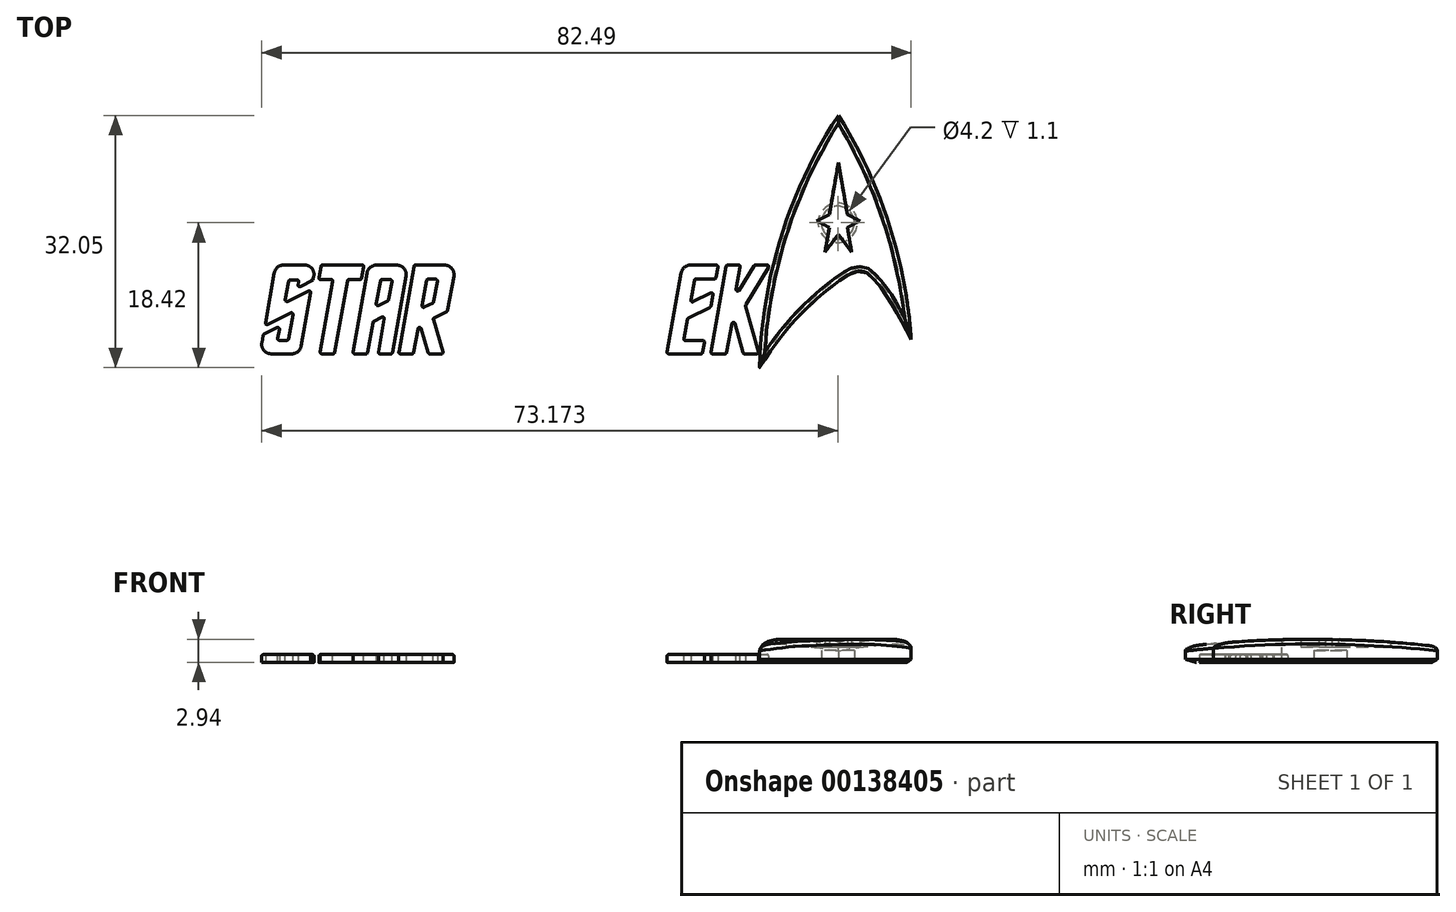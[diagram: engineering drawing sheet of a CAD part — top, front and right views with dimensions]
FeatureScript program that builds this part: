
annotation { "Feature Type Name" : "Feature", "Feature Type Description" : "" }
export const myFeature = defineFeature(function(context is Context, id is Id, definition is map)
    precondition{}
    {
        {
            var Q0;
            Q0=qCreatedBy(makeId("Top.planeOp"),FACE);
            var sketch = newSketch(context, id + "F0", { "sketchPlane" : qUnion([Q0])});
            skLineSegment(sketch, "E0", {"start": v(-63.47, 1.77) * mm, "end": v(-63.04, 4.22) * mm});
            skLineSegment(sketch, "E1", {"start": v(-61.48, 13.05) * mm, "end": v(-56.38, 13.05) * mm});
            skLineSegment(sketch, "E2", {"start": v(-56.38, 13.05) * mm, "end": v(-56.71, 11.14) * mm});
            skLineSegment(sketch, "E3", {"start": v(-56.71, 11.14) * mm, "end": v(-58.7, 10.14) * mm});
            skLineSegment(sketch, "E4", {"start": v(-58.7, 10.14) * mm, "end": v(-58.52, 11.14) * mm});
            skLineSegment(sketch, "E5", {"start": v(-58.52, 11.14) * mm, "end": v(-59.8, 11.14) * mm});
            skLineSegment(sketch, "E6", {"start": v(-59.8, 11.14) * mm, "end": v(-60.32, 8.24) * mm});
            skLineSegment(sketch, "E7", {"start": v(-60.32, 8.24) * mm, "end": v(-56.96, 9.93) * mm});
            skLineSegment(sketch, "E8", {"start": v(-56.96, 9.93) * mm, "end": v(-58.4, 1.77) * mm});
            skLineSegment(sketch, "E9", {"start": v(-58.4, 1.77) * mm, "end": v(-63.47, 1.77) * mm});
            skLineSegment(sketch, "E10", {"start": v(-59.86, 3.49) * mm, "end": v(-59.21, 7.15) * mm});
            skLineSegment(sketch, "E11", {"start": v(-59.21, 7.15) * mm, "end": v(-62.85, 5.31) * mm});
            skLineSegment(sketch, "E12", {"start": v(-63.04, 4.22) * mm, "end": v(-60.94, 5.28) * mm});
            skLineSegment(sketch, "E13", {"start": v(-60.94, 5.28) * mm, "end": v(-61.25, 3.49) * mm});
            skLineSegment(sketch, "E14", {"start": v(-61.25, 3.49) * mm, "end": v(-59.86, 3.49) * mm});
            skLineSegment(sketch, "E15", {"start": v(-55.7, 13.04) * mm, "end": v(-57.69, 1.77) * mm});
            skLineSegment(sketch, "E16", {"start": v(-55.85, 1.77) * mm, "end": v(-54, 1.77) * mm});
            skLineSegment(sketch, "E17", {"start": v(-52.25, 1.77) * mm, "end": v(-50.25, 13.04) * mm});
            skLineSegment(sketch, "E18", {"start": v(-55.7, 13.04) * mm, "end": v(-50.25, 13.04) * mm});
            skLineSegment(sketch, "E19", {"start": v(-55.85, 1.77) * mm, "end": v(-54.18, 11.21) * mm});
            skLineSegment(sketch, "E20", {"start": v(-54.18, 11.21) * mm, "end": v(-56.02, 11.21) * mm});
            skLineSegment(sketch, "E21", {"start": v(-54, 1.77) * mm, "end": v(-52.32, 11.21) * mm});
            skLineSegment(sketch, "E22", {"start": v(-52.32, 11.21) * mm, "end": v(-50.57, 11.21) * mm});
            skLineSegment(sketch, "E23", {"start": v(-51.68, 1.77) * mm, "end": v(-49.68, 13.04) * mm});
            skLineSegment(sketch, "E24", {"start": v(-49.68, 13.04) * mm, "end": v(-44.67, 13.04) * mm});
            skLineSegment(sketch, "E25", {"start": v(-44.67, 13.04) * mm, "end": v(-46.66, 1.77) * mm});
            skLineSegment(sketch, "E26", {"start": v(-46.66, 1.77) * mm, "end": v(-48.47, 1.77) * mm});
            skLineSegment(sketch, "E27", {"start": v(-45.87, 1.77) * mm, "end": v(-43.87, 13.04) * mm});
            skLineSegment(sketch, "E28", {"start": v(-43.87, 13.04) * mm, "end": v(-38.6, 13.04) * mm});
            skLineSegment(sketch, "E29", {"start": v(-38.6, 13.04) * mm, "end": v(-39.63, 7.21) * mm});
            skLineSegment(sketch, "E30", {"start": v(-40.42, 2.74) * mm, "end": v(-40.12, 1.77) * mm});
            skLineSegment(sketch, "E31", {"start": v(-40.12, 1.77) * mm, "end": v(-42.07, 1.77) * mm});
            skLineSegment(sketch, "E32", {"start": v(-40.42, 2.74) * mm, "end": v(-41.5, 6.27) * mm});
            skLineSegment(sketch, "E33", {"start": v(-49.82, 1.77) * mm, "end": v(-49.1, 5.85) * mm});
            skLineSegment(sketch, "E34", {"start": v(-49.1, 5.85) * mm, "end": v(-47.61, 6.6) * mm});
            skLineSegment(sketch, "E35", {"start": v(-47.61, 6.6) * mm, "end": v(-48.47, 1.77) * mm});
            skLineSegment(sketch, "E36", {"start": v(-41.5, 6.27) * mm, "end": v(-39.63, 7.21) * mm});
            skLineSegment(sketch, "E37", {"start": v(-43.26, 5.78) * mm, "end": v(-43.97, 1.77) * mm});
            skLineSegment(sketch, "E38", {"start": v(-42.07, 1.77) * mm, "end": v(-43.26, 5.78) * mm});
            skLineSegment(sketch, "E39", {"start": v(-42.95, 7.51) * mm, "end": v(-41.41, 8.3) * mm});
            skLineSegment(sketch, "E40", {"start": v(-41.41, 8.3) * mm, "end": v(-40.9, 11.24) * mm});
            skLineSegment(sketch, "E41", {"start": v(-42.95, 7.51) * mm, "end": v(-42.3, 11.24) * mm});
            skLineSegment(sketch, "E42", {"start": v(-42.3, 11.24) * mm, "end": v(-40.9, 11.24) * mm});
            skLineSegment(sketch, "E43.trimOffspring", {"start": v(-43.97, 1.77) * mm, "end": v(-45.87, 1.77) * mm});
            skLineSegment(sketch, "E44", {"start": v(-48.76, 7.72) * mm, "end": v(-48.15, 11.21) * mm});
            skLineSegment(sketch, "E45", {"start": v(-48.15, 11.21) * mm, "end": v(-46.67, 11.21) * mm});
            skLineSegment(sketch, "E46", {"start": v(-46.67, 11.21) * mm, "end": v(-47.15, 8.54) * mm});
            skLineSegment(sketch, "E47", {"start": v(-48.76, 7.72) * mm, "end": v(-47.15, 8.54) * mm});
            skLineSegment(sketch, "E48.trimOffspring", {"start": v(-62.85, 5.31) * mm, "end": v(-61.48, 13.05) * mm});
            skLineSegment(sketch, "E49.trimOffspring", {"start": v(-49.82, 1.77) * mm, "end": v(-51.68, 1.77) * mm});
            skLineSegment(sketch, "E50", {"start": v(-9.8, 13.04) * mm, "end": v(-11.8, 1.77) * mm});
            skLineSegment(sketch, "E51", {"start": v(-11.8, 1.77) * mm, "end": v(-7.25, 1.77) * mm});
            skLineSegment(sketch, "E52", {"start": v(-7.25, 1.77) * mm, "end": v(-6.95, 3.45) * mm});
            skLineSegment(sketch, "E53", {"start": v(-5.26, 13.04) * mm, "end": v(-9.8, 13.04) * mm});
            skLineSegment(sketch, "E54", {"start": v(-6.23, 1.77) * mm, "end": v(-4.23, 13.04) * mm});
            skLineSegment(sketch, "E55", {"start": v(-4.23, 13.04) * mm, "end": v(-2.43, 13.04) * mm});
            skLineSegment(sketch, "E56", {"start": v(-0.45, 3.06) * mm, "end": v(-0.1, 1.77) * mm});
            skLineSegment(sketch, "E57", {"start": v(-0.1, 1.77) * mm, "end": v(-2.08, 1.77) * mm});
            skLineSegment(sketch, "E58", {"start": v(-0.45, 3.06) * mm, "end": v(-1.79, 7.94) * mm});
            skLineSegment(sketch, "E59", {"start": v(-1.79, 7.94) * mm, "end": v(1.32, 13.04) * mm});
            skLineSegment(sketch, "E60", {"start": v(-0.64, 13.04) * mm, "end": v(-3.16, 8.91) * mm});
            skLineSegment(sketch, "E61", {"start": v(-3.16, 8.91) * mm, "end": v(-2.43, 13.04) * mm});
            skLineSegment(sketch, "E62", {"start": v(-4.2, 1.77) * mm, "end": v(-3.37, 6.47) * mm});
            skLineSegment(sketch, "E63", {"start": v(-3.37, 6.47) * mm, "end": v(-2.08, 1.77) * mm});
            skLineSegment(sketch, "E64", {"start": v(-6.95, 3.45) * mm, "end": v(-9.64, 3.45) * mm});
            skLineSegment(sketch, "E65", {"start": v(-9.64, 3.45) * mm, "end": v(-9.14, 6.27) * mm});
            skLineSegment(sketch, "E66", {"start": v(-9.14, 6.27) * mm, "end": v(-6.2, 7.72) * mm});
            skLineSegment(sketch, "E67", {"start": v(-9.14, 6.27) * mm, "end": v(-8.26, 11.26) * mm});
            skLineSegment(sketch, "E68", {"start": v(-8.26, 11.26) * mm, "end": v(-5.57, 11.26) * mm});
            skLineSegment(sketch, "E69", {"start": v(-8.8, 8.2) * mm, "end": v(-5.85, 9.67) * mm});
            skLineSegment(sketch, "E70.trimOffspring", {"start": v(-5.57, 11.26) * mm, "end": v(-5.26, 13.04) * mm});
            skLineSegment(sketch, "E71.trimOffspring", {"start": v(-6.2, 7.72) * mm, "end": v(-5.85, 9.67) * mm});
            skLineSegment(sketch, "E72.trimOffspring", {"start": v(-4.2, 1.77) * mm, "end": v(-6.23, 1.77) * mm});
            skLineSegment(sketch, "E73.trimOffspring", {"start": v(-0.64, 13.04) * mm, "end": v(1.32, 13.04) * mm});
            skSolve(sketch);
        }
        {
            var Q0;
            Q0 = qSketchRegion(id + "F0", true);
            extrude(context, id + "F1", {"entities" : qUnion([Q0]), "depth" : 1 * mm, "offsetDistance" : 25 * mm});
        }
        {
            var Q0;
            Q0=makeQuery(id+"F1.opExtrude","SWEPT_EDGE",EDGE,{"disambiguationData":[OSD([sQuery(id+"F0.wireOp",EDGE,"E8"),sQuery(id+"F0.wireOp",EDGE,"E9")])]});
            var Q1;
            Q1=makeQuery(id+"F1.opExtrude","SWEPT_EDGE",EDGE,{"disambiguationData":[OSD([sQuery(id+"F0.wireOp",EDGE,"E0"),sQuery(id+"F0.wireOp",EDGE,"E9")])]});
            var Q2;
            Q2=makeQuery(id+"F1.opExtrude","SWEPT_EDGE",EDGE,{"disambiguationData":[OSD([sQuery(id+"F0.wireOp",EDGE,"E1"),sQuery(id+"F0.wireOp",EDGE,"E48.trimOffspring")])]});
            var Q3;
            Q3=makeQuery(id+"F1.opExtrude","SWEPT_EDGE",EDGE,{"disambiguationData":[OSD([sQuery(id+"F0.wireOp",EDGE,"E1"),sQuery(id+"F0.wireOp",EDGE,"E2")])]});
            var Q4;
            Q4=makeQuery(id+"F1.opExtrude","SWEPT_EDGE",EDGE,{"disambiguationData":[OSD([sQuery(id+"F0.wireOp",EDGE,"E23"),sQuery(id+"F0.wireOp",EDGE,"E24")])]});
            var Q5;
            Q5=makeQuery(id+"F1.opExtrude","SWEPT_EDGE",EDGE,{"disambiguationData":[OSD([sQuery(id+"F0.wireOp",EDGE,"E24"),sQuery(id+"F0.wireOp",EDGE,"E25")])]});
            var Q6;
            Q6=makeQuery(id+"F1.opExtrude","SWEPT_EDGE",EDGE,{"disambiguationData":[OSD([sQuery(id+"F0.wireOp",EDGE,"E28"),sQuery(id+"F0.wireOp",EDGE,"E29")])]});
            var Q7;
            Q7=makeQuery(id+"F1.opExtrude","SWEPT_EDGE",EDGE,{"disambiguationData":[OSD([sQuery(id+"F0.wireOp",EDGE,"E50"),sQuery(id+"F0.wireOp",EDGE,"E53")])]});
            fillet(context, id + "F2", {"entities" : qUnion([Q0, Q1, Q2, Q3, Q4, Q5, Q6, Q7]), "tangentPropagation" : true, "radius" : 1.2 * mm, "defaultsChanged" : false, "vertexSettings" : [], "allowEdgeOverflow" : false});
        }
        {
            var Q0;
            Q0=makeQuery(id+"F1.opExtrude","SWEPT_EDGE",EDGE,{"disambiguationData":[OSD([sQuery(id+"F0.wireOp",EDGE,"E7"),sQuery(id+"F0.wireOp",EDGE,"E8")])]});
            var Q1;
            Q1=makeQuery(id+"F1.opExtrude","SWEPT_EDGE",EDGE,{"disambiguationData":[OSD([sQuery(id+"F0.wireOp",EDGE,"E3"),sQuery(id+"F0.wireOp",EDGE,"E4")])]});
            var Q2;
            Q2=makeQuery(id+"F1.opExtrude","SWEPT_EDGE",EDGE,{"disambiguationData":[OSD([sQuery(id+"F0.wireOp",EDGE,"E5"),sQuery(id+"F0.wireOp",EDGE,"E6")])]});
            var Q3;
            Q3=makeQuery(id+"F1.opExtrude","SWEPT_EDGE",EDGE,{"disambiguationData":[OSD([sQuery(id+"F0.wireOp",EDGE,"E6"),sQuery(id+"F0.wireOp",EDGE,"E7")])]});
            var Q4;
            Q4=makeQuery(id+"F1.opExtrude","SWEPT_EDGE",EDGE,{"disambiguationData":[OSD([sQuery(id+"F0.wireOp",EDGE,"E13"),sQuery(id+"F0.wireOp",EDGE,"E14")])]});
            var Q5;
            Q5=makeQuery(id+"F1.opExtrude","SWEPT_EDGE",EDGE,{"disambiguationData":[OSD([sQuery(id+"F0.wireOp",EDGE,"E12"),sQuery(id+"F0.wireOp",EDGE,"E13")])]});
            var Q6;
            Q6=makeQuery(id+"F1.opExtrude","SWEPT_EDGE",EDGE,{"disambiguationData":[OSD([sQuery(id+"F0.wireOp",EDGE,"E0"),sQuery(id+"F0.wireOp",EDGE,"E12")])]});
            var Q7;
            Q7=makeQuery(id+"F1.opExtrude","SWEPT_EDGE",EDGE,{"disambiguationData":[OSD([sQuery(id+"F0.wireOp",EDGE,"E10"),sQuery(id+"F0.wireOp",EDGE,"E14")])]});
            var Q8;
            Q8=makeQuery(id+"F1.opExtrude","SWEPT_EDGE",EDGE,{"disambiguationData":[OSD([sQuery(id+"F0.wireOp",EDGE,"E10"),sQuery(id+"F0.wireOp",EDGE,"E11")])]});
            var Q9;
            Q9=makeQuery(id+"F1.opExtrude","SWEPT_EDGE",EDGE,{"disambiguationData":[OSD([sQuery(id+"F0.wireOp",EDGE,"E11"),sQuery(id+"F0.wireOp",EDGE,"E48.trimOffspring")])]});
            var Q10;
            Q10=makeQuery(id+"F1.opExtrude","SWEPT_EDGE",EDGE,{"disambiguationData":[OSD([sQuery(id+"F0.wireOp",EDGE,"E4"),sQuery(id+"F0.wireOp",EDGE,"E5")])]});
            var Q11;
            Q11=makeQuery(id+"F1.opExtrude","SWEPT_EDGE",EDGE,{"disambiguationData":[OSD([sQuery(id+"F0.wireOp",EDGE,"E15"),sQuery(id+"F0.wireOp",EDGE,"E18")])]});
            var Q12;
            Q12=makeQuery(id+"F1.opExtrude","SWEPT_EDGE",EDGE,{"disambiguationData":[OSD([sQuery(id+"F0.wireOp",EDGE,"E15"),sQuery(id+"F0.wireOp",EDGE,"E20")])]});
            var Q13;
            Q13=makeQuery(id+"F1.opExtrude","SWEPT_EDGE",EDGE,{"disambiguationData":[OSD([sQuery(id+"F0.wireOp",EDGE,"E19"),sQuery(id+"F0.wireOp",EDGE,"E20")])]});
            var Q14;
            Q14=makeQuery(id+"F1.opExtrude","SWEPT_EDGE",EDGE,{"disambiguationData":[OSD([sQuery(id+"F0.wireOp",EDGE,"E16"),sQuery(id+"F0.wireOp",EDGE,"E19")])]});
            var Q15;
            Q15=makeQuery(id+"F1.opExtrude","SWEPT_EDGE",EDGE,{"disambiguationData":[OSD([sQuery(id+"F0.wireOp",EDGE,"E16"),sQuery(id+"F0.wireOp",EDGE,"E21")])]});
            var Q16;
            Q16=makeQuery(id+"F1.opExtrude","SWEPT_EDGE",EDGE,{"disambiguationData":[OSD([sQuery(id+"F0.wireOp",EDGE,"E21"),sQuery(id+"F0.wireOp",EDGE,"E22")])]});
            var Q17;
            Q17=makeQuery(id+"F1.opExtrude","SWEPT_EDGE",EDGE,{"disambiguationData":[OSD([sQuery(id+"F0.wireOp",EDGE,"E17"),sQuery(id+"F0.wireOp",EDGE,"E22")])]});
            var Q18;
            Q18=makeQuery(id+"F1.opExtrude","SWEPT_EDGE",EDGE,{"disambiguationData":[OSD([sQuery(id+"F0.wireOp",EDGE,"E17"),sQuery(id+"F0.wireOp",EDGE,"E18")])]});
            var Q19;
            Q19=makeQuery(id+"F1.opExtrude","SWEPT_EDGE",EDGE,{"disambiguationData":[OSD([sQuery(id+"F0.wireOp",EDGE,"E44"),sQuery(id+"F0.wireOp",EDGE,"E45")])]});
            var Q20;
            Q20=makeQuery(id+"F1.opExtrude","SWEPT_EDGE",EDGE,{"disambiguationData":[OSD([sQuery(id+"F0.wireOp",EDGE,"E23"),sQuery(id+"F0.wireOp",EDGE,"E49.trimOffspring")])]});
            var Q21;
            Q21=makeQuery(id+"F1.opExtrude","SWEPT_EDGE",EDGE,{"disambiguationData":[OSD([sQuery(id+"F0.wireOp",EDGE,"E26"),sQuery(id+"F0.wireOp",EDGE,"E35")])]});
            var Q22;
            Q22=makeQuery(id+"F1.opExtrude","SWEPT_EDGE",EDGE,{"disambiguationData":[OSD([sQuery(id+"F0.wireOp",EDGE,"E33"),sQuery(id+"F0.wireOp",EDGE,"E49.trimOffspring")])]});
            var Q23;
            Q23=makeQuery(id+"F1.opExtrude","SWEPT_EDGE",EDGE,{"disambiguationData":[OSD([sQuery(id+"F0.wireOp",EDGE,"E33"),sQuery(id+"F0.wireOp",EDGE,"E34")])]});
            var Q24;
            Q24=makeQuery(id+"F1.opExtrude","SWEPT_EDGE",EDGE,{"disambiguationData":[OSD([sQuery(id+"F0.wireOp",EDGE,"E34"),sQuery(id+"F0.wireOp",EDGE,"E35")])]});
            var Q25;
            Q25=makeQuery(id+"F1.opExtrude","SWEPT_EDGE",EDGE,{"disambiguationData":[OSD([sQuery(id+"F0.wireOp",EDGE,"E25"),sQuery(id+"F0.wireOp",EDGE,"E26")])]});
            var Q26;
            Q26=makeQuery(id+"F1.opExtrude","SWEPT_EDGE",EDGE,{"disambiguationData":[OSD([sQuery(id+"F0.wireOp",EDGE,"E46"),sQuery(id+"F0.wireOp",EDGE,"E47")])]});
            var Q27;
            Q27=makeQuery(id+"F1.opExtrude","SWEPT_EDGE",EDGE,{"disambiguationData":[OSD([sQuery(id+"F0.wireOp",EDGE,"E45"),sQuery(id+"F0.wireOp",EDGE,"E46")])]});
            var Q28;
            Q28=makeQuery(id+"F1.opExtrude","SWEPT_EDGE",EDGE,{"disambiguationData":[OSD([sQuery(id+"F0.wireOp",EDGE,"E44"),sQuery(id+"F0.wireOp",EDGE,"E47")])]});
            var Q29;
            Q29=makeQuery(id+"F1.opExtrude","SWEPT_EDGE",EDGE,{"disambiguationData":[OSD([sQuery(id+"F0.wireOp",EDGE,"E27"),sQuery(id+"F0.wireOp",EDGE,"E43.trimOffspring")])]});
            var Q30;
            Q30=makeQuery(id+"F1.opExtrude","SWEPT_EDGE",EDGE,{"disambiguationData":[OSD([sQuery(id+"F0.wireOp",EDGE,"E37"),sQuery(id+"F0.wireOp",EDGE,"E43.trimOffspring")])]});
            var Q31;
            Q31=makeQuery(id+"F1.opExtrude","SWEPT_EDGE",EDGE,{"disambiguationData":[OSD([sQuery(id+"F0.wireOp",EDGE,"E31"),sQuery(id+"F0.wireOp",EDGE,"E38")])]});
            var Q32;
            Q32=makeQuery(id+"F1.opExtrude","SWEPT_EDGE",EDGE,{"disambiguationData":[OSD([sQuery(id+"F0.wireOp",EDGE,"E30"),sQuery(id+"F0.wireOp",EDGE,"E31")])]});
            var Q33;
            Q33=makeQuery(id+"F1.opExtrude","SWEPT_EDGE",EDGE,{"disambiguationData":[OSD([sQuery(id+"F0.wireOp",EDGE,"E32"),sQuery(id+"F0.wireOp",EDGE,"E36")])]});
            var Q34;
            Q34=makeQuery(id+"F1.opExtrude","SWEPT_EDGE",EDGE,{"disambiguationData":[OSD([sQuery(id+"F0.wireOp",EDGE,"E29"),sQuery(id+"F0.wireOp",EDGE,"E36")])]});
            var Q35;
            Q35=makeQuery(id+"F1.opExtrude","SWEPT_EDGE",EDGE,{"disambiguationData":[OSD([sQuery(id+"F0.wireOp",EDGE,"E41"),sQuery(id+"F0.wireOp",EDGE,"E42")])]});
            var Q36;
            Q36=makeQuery(id+"F1.opExtrude","SWEPT_EDGE",EDGE,{"disambiguationData":[OSD([sQuery(id+"F0.wireOp",EDGE,"E37"),sQuery(id+"F0.wireOp",EDGE,"E38")])]});
            var Q37;
            Q37=makeQuery(id+"F1.opExtrude","SWEPT_EDGE",EDGE,{"disambiguationData":[OSD([sQuery(id+"F0.wireOp",EDGE,"E39"),sQuery(id+"F0.wireOp",EDGE,"E40")])]});
            var Q38;
            Q38=makeQuery(id+"F1.opExtrude","SWEPT_EDGE",EDGE,{"disambiguationData":[OSD([sQuery(id+"F0.wireOp",EDGE,"E39"),sQuery(id+"F0.wireOp",EDGE,"E41")])]});
            var Q39;
            Q39=makeQuery(id+"F1.opExtrude","SWEPT_EDGE",EDGE,{"disambiguationData":[OSD([sQuery(id+"F0.wireOp",EDGE,"E40"),sQuery(id+"F0.wireOp",EDGE,"E42")])]});
            var Q40;
            Q40=makeQuery(id+"F1.opExtrude","SWEPT_EDGE",EDGE,{"disambiguationData":[OSD([sQuery(id+"F0.wireOp",EDGE,"E27"),sQuery(id+"F0.wireOp",EDGE,"E28")])]});
            var Q41;
            Q41=makeQuery(id+"F1.opExtrude","SWEPT_EDGE",EDGE,{"disambiguationData":[OSD([sQuery(id+"F0.wireOp",EDGE,"E53"),sQuery(id+"F0.wireOp",EDGE,"E70.trimOffspring")])]});
            var Q42;
            Q42=makeQuery(id+"F1.opExtrude","SWEPT_EDGE",EDGE,{"disambiguationData":[OSD([sQuery(id+"F0.wireOp",EDGE,"E68"),sQuery(id+"F0.wireOp",EDGE,"E70.trimOffspring")])]});
            var Q43;
            Q43=makeQuery(id+"F1.opExtrude","SWEPT_EDGE",EDGE,{"disambiguationData":[OSD([sQuery(id+"F0.wireOp",EDGE,"E69"),sQuery(id+"F0.wireOp",EDGE,"E71.trimOffspring")])]});
            var Q44;
            Q44=makeQuery(id+"F1.opExtrude","SWEPT_EDGE",EDGE,{"disambiguationData":[OSD([sQuery(id+"F0.wireOp",EDGE,"E66"),sQuery(id+"F0.wireOp",EDGE,"E71.trimOffspring")])]});
            var Q45;
            Q45=makeQuery(id+"F1.opExtrude","SWEPT_EDGE",EDGE,{"disambiguationData":[OSD([sQuery(id+"F0.wireOp",EDGE,"E67"),sQuery(id+"F0.wireOp",EDGE,"E68")])]});
            var Q46;
            Q46=makeQuery(id+"F1.opExtrude","SWEPT_EDGE",EDGE,{"disambiguationData":[OSD([sQuery(id+"F0.wireOp",EDGE,"E67"),sQuery(id+"F0.wireOp",EDGE,"E69")])]});
            var Q47;
            Q47=makeQuery(id+"F1.opExtrude","SWEPT_EDGE",EDGE,{"disambiguationData":[OSD([sQuery(id+"F0.wireOp",EDGE,"E65"),sQuery(id+"F0.wireOp",EDGE,"E66"),sQuery(id+"F0.wireOp",EDGE,"E67")])]});
            var Q48;
            Q48=makeQuery(id+"F1.opExtrude","SWEPT_EDGE",EDGE,{"disambiguationData":[OSD([sQuery(id+"F0.wireOp",EDGE,"E52"),sQuery(id+"F0.wireOp",EDGE,"E64")])]});
            var Q49;
            Q49=makeQuery(id+"F1.opExtrude","SWEPT_EDGE",EDGE,{"disambiguationData":[OSD([sQuery(id+"F0.wireOp",EDGE,"E51"),sQuery(id+"F0.wireOp",EDGE,"E52")])]});
            var Q50;
            Q50=makeQuery(id+"F1.opExtrude","SWEPT_EDGE",EDGE,{"disambiguationData":[OSD([sQuery(id+"F0.wireOp",EDGE,"E50"),sQuery(id+"F0.wireOp",EDGE,"E51")])]});
            var Q51;
            Q51=makeQuery(id+"F1.opExtrude","SWEPT_EDGE",EDGE,{"disambiguationData":[OSD([sQuery(id+"F0.wireOp",EDGE,"E64"),sQuery(id+"F0.wireOp",EDGE,"E65")])]});
            var Q52;
            Q52=makeQuery(id+"F1.opExtrude","SWEPT_EDGE",EDGE,{"disambiguationData":[OSD([sQuery(id+"F0.wireOp",EDGE,"E62"),sQuery(id+"F0.wireOp",EDGE,"E63")])]});
            var Q53;
            Q53=makeQuery(id+"F1.opExtrude","SWEPT_EDGE",EDGE,{"disambiguationData":[OSD([sQuery(id+"F0.wireOp",EDGE,"E62"),sQuery(id+"F0.wireOp",EDGE,"E72.trimOffspring")])]});
            var Q54;
            Q54=makeQuery(id+"F1.opExtrude","SWEPT_EDGE",EDGE,{"disambiguationData":[OSD([sQuery(id+"F0.wireOp",EDGE,"E54"),sQuery(id+"F0.wireOp",EDGE,"E72.trimOffspring")])]});
            var Q55;
            Q55=makeQuery(id+"F1.opExtrude","SWEPT_EDGE",EDGE,{"disambiguationData":[OSD([sQuery(id+"F0.wireOp",EDGE,"E57"),sQuery(id+"F0.wireOp",EDGE,"E63")])]});
            var Q56;
            Q56=makeQuery(id+"F1.opExtrude","SWEPT_EDGE",EDGE,{"disambiguationData":[OSD([sQuery(id+"F0.wireOp",EDGE,"E56"),sQuery(id+"F0.wireOp",EDGE,"E57")])]});
            var Q57;
            Q57=makeQuery(id+"F1.opExtrude","SWEPT_EDGE",EDGE,{"disambiguationData":[OSD([sQuery(id+"F0.wireOp",EDGE,"E58"),sQuery(id+"F0.wireOp",EDGE,"E59")])]});
            var Q58;
            Q58=makeQuery(id+"F1.opExtrude","SWEPT_EDGE",EDGE,{"disambiguationData":[OSD([sQuery(id+"F0.wireOp",EDGE,"E59"),sQuery(id+"F0.wireOp",EDGE,"E73.trimOffspring")])]});
            var Q59;
            Q59=makeQuery(id+"F1.opExtrude","SWEPT_EDGE",EDGE,{"disambiguationData":[OSD([sQuery(id+"F0.wireOp",EDGE,"E60"),sQuery(id+"F0.wireOp",EDGE,"E73.trimOffspring")])]});
            var Q60;
            Q60=makeQuery(id+"F1.opExtrude","SWEPT_EDGE",EDGE,{"disambiguationData":[OSD([sQuery(id+"F0.wireOp",EDGE,"E60"),sQuery(id+"F0.wireOp",EDGE,"E61")])]});
            var Q61;
            Q61=makeQuery(id+"F1.opExtrude","SWEPT_EDGE",EDGE,{"disambiguationData":[OSD([sQuery(id+"F0.wireOp",EDGE,"E55"),sQuery(id+"F0.wireOp",EDGE,"E61")])]});
            var Q62;
            Q62=makeQuery(id+"F1.opExtrude","SWEPT_EDGE",EDGE,{"disambiguationData":[OSD([sQuery(id+"F0.wireOp",EDGE,"E54"),sQuery(id+"F0.wireOp",EDGE,"E55")])]});
            fillet(context, id + "F3", {"entities" : qUnion([Q0, Q1, Q2, Q3, Q4, Q5, Q6, Q7, Q8, Q9, Q10, Q11, Q12, Q13, Q14, Q15, Q16, Q17, Q18, Q19, Q20, Q21, Q22, Q23, Q24, Q25, Q26, Q27, Q28, Q29, Q30, Q31, Q32, Q33, Q34, Q35, Q36, Q37, Q38, Q39, Q40, Q41, Q42, Q43, Q44, Q45, Q46, Q47, Q48, Q49, Q50, Q51, Q52, Q53, Q54, Q55, Q56, Q57, Q58, Q59, Q60, Q61, Q62]), "tangentPropagation" : true, "radius" : 0.2 * mm, "defaultsChanged" : false, "vertexSettings" : [], "allowEdgeOverflow" : false});
        }
        {
            var Q0;
            Q0=makeQuery(id+"F1.opExtrude","CAP_FACE",FACE,{"disambiguationData":[OSD([sQuery(id+"F0.wireOp",EDGE,"E0"),sQuery(id+"F0.wireOp",EDGE,"E1"),sQuery(id+"F0.wireOp",EDGE,"E2"),sQuery(id+"F0.wireOp",EDGE,"E3"),sQuery(id+"F0.wireOp",EDGE,"E4"),sQuery(id+"F0.wireOp",EDGE,"E5"),sQuery(id+"F0.wireOp",EDGE,"E6"),sQuery(id+"F0.wireOp",EDGE,"E7"),sQuery(id+"F0.wireOp",EDGE,"E8"),sQuery(id+"F0.wireOp",EDGE,"E9"),sQuery(id+"F0.wireOp",EDGE,"E10"),sQuery(id+"F0.wireOp",EDGE,"E11"),sQuery(id+"F0.wireOp",EDGE,"E12"),sQuery(id+"F0.wireOp",EDGE,"E13"),sQuery(id+"F0.wireOp",EDGE,"E14"),sQuery(id+"F0.wireOp",EDGE,"E48.trimOffspring")])],"isStart":false});
            var Q1;
            Q1=makeQuery(id+"F1.opExtrude","CAP_FACE",FACE,{"disambiguationData":[OSD([sQuery(id+"F0.wireOp",EDGE,"E15"),sQuery(id+"F0.wireOp",EDGE,"E16"),sQuery(id+"F0.wireOp",EDGE,"E17"),sQuery(id+"F0.wireOp",EDGE,"E18"),sQuery(id+"F0.wireOp",EDGE,"E19"),sQuery(id+"F0.wireOp",EDGE,"E20"),sQuery(id+"F0.wireOp",EDGE,"E21"),sQuery(id+"F0.wireOp",EDGE,"E22")])],"isStart":false});
            var Q2;
            Q2=makeQuery(id+"F1.opExtrude","CAP_FACE",FACE,{"disambiguationData":[OSD([sQuery(id+"F0.wireOp",EDGE,"E23"),sQuery(id+"F0.wireOp",EDGE,"E24"),sQuery(id+"F0.wireOp",EDGE,"E25"),sQuery(id+"F0.wireOp",EDGE,"E26"),sQuery(id+"F0.wireOp",EDGE,"E33"),sQuery(id+"F0.wireOp",EDGE,"E34"),sQuery(id+"F0.wireOp",EDGE,"E35"),sQuery(id+"F0.wireOp",EDGE,"E44"),sQuery(id+"F0.wireOp",EDGE,"E45"),sQuery(id+"F0.wireOp",EDGE,"E46"),sQuery(id+"F0.wireOp",EDGE,"E47"),sQuery(id+"F0.wireOp",EDGE,"E49.trimOffspring")])],"isStart":false});
            var Q3;
            Q3=makeQuery(id+"F1.opExtrude","CAP_FACE",FACE,{"disambiguationData":[OSD([sQuery(id+"F0.wireOp",EDGE,"E27"),sQuery(id+"F0.wireOp",EDGE,"E28"),sQuery(id+"F0.wireOp",EDGE,"E29"),sQuery(id+"F0.wireOp",EDGE,"E30"),sQuery(id+"F0.wireOp",EDGE,"E31"),sQuery(id+"F0.wireOp",EDGE,"E32"),sQuery(id+"F0.wireOp",EDGE,"E36"),sQuery(id+"F0.wireOp",EDGE,"E37"),sQuery(id+"F0.wireOp",EDGE,"E38"),sQuery(id+"F0.wireOp",EDGE,"E39"),sQuery(id+"F0.wireOp",EDGE,"E40"),sQuery(id+"F0.wireOp",EDGE,"E41"),sQuery(id+"F0.wireOp",EDGE,"E42"),sQuery(id+"F0.wireOp",EDGE,"E43.trimOffspring")])],"isStart":false});
            var Q4;
            Q4=makeQuery(id+"F1.opExtrude","CAP_FACE",FACE,{"disambiguationData":[OSD([sQuery(id+"F0.wireOp",EDGE,"E50"),sQuery(id+"F0.wireOp",EDGE,"E51"),sQuery(id+"F0.wireOp",EDGE,"E52"),sQuery(id+"F0.wireOp",EDGE,"E53"),sQuery(id+"F0.wireOp",EDGE,"E64"),sQuery(id+"F0.wireOp",EDGE,"E65"),sQuery(id+"F0.wireOp",EDGE,"E66"),sQuery(id+"F0.wireOp",EDGE,"E67"),sQuery(id+"F0.wireOp",EDGE,"E68"),sQuery(id+"F0.wireOp",EDGE,"E69"),sQuery(id+"F0.wireOp",EDGE,"E70.trimOffspring"),sQuery(id+"F0.wireOp",EDGE,"E71.trimOffspring")])],"isStart":false});
            var Q5;
            Q5=makeQuery(id+"F1.opExtrude","CAP_FACE",FACE,{"disambiguationData":[OSD([sQuery(id+"F0.wireOp",EDGE,"E54"),sQuery(id+"F0.wireOp",EDGE,"E55"),sQuery(id+"F0.wireOp",EDGE,"E56"),sQuery(id+"F0.wireOp",EDGE,"E57"),sQuery(id+"F0.wireOp",EDGE,"E58"),sQuery(id+"F0.wireOp",EDGE,"E59"),sQuery(id+"F0.wireOp",EDGE,"E60"),sQuery(id+"F0.wireOp",EDGE,"E61"),sQuery(id+"F0.wireOp",EDGE,"E62"),sQuery(id+"F0.wireOp",EDGE,"E63"),sQuery(id+"F0.wireOp",EDGE,"E72.trimOffspring"),sQuery(id+"F0.wireOp",EDGE,"E73.trimOffspring")])],"isStart":false});
            fillet(context, id + "F4", {"entities" : qUnion([Q0, Q1, Q2, Q3, Q4, Q5]), "tangentPropagation" : true, "radius" : 0.2 * mm, "defaultsChanged" : false, "vertexSettings" : [], "allowEdgeOverflow" : false});
        }
        {
            var Q0;
            Q0=qCreatedBy(makeId("Top.planeOp"),FACE);
            var sketch = newSketch(context, id + "F5", { "sketchPlane" : qUnion([Q0])});
            skArc(sketch, "E74", {"start": v(10, 32.05) * mm, "mid": v(2.75, 16.73) * mm, "end": v(0, 0) * mm});
            skArc(sketch, "E75", {"start": v(19.25, 3.58) * mm, "mid": v(16.4, 18.4) * mm, "end": v(10, 32.05) * mm});
            skFitSpline(sketch, "E76", {"points": [v(19.25, 3.58) * mm, v(17.29, 7.18) * mm, v(15.43, 10.15) * mm, v(14.23, 11.51) * mm, v(13.29, 12.2) * mm, v(11.98, 12.12) * mm, v(10.29, 11.18) * mm, v(5.93, 7.51) * mm, v(2.46, 3.58) * mm, v(0, 0) * mm], "startDerivative": vector(-14.26, 27.94) * mm, "endDerivative": vector(-17.6, -27.28) * mm});
            skSolve(sketch);
        }
        {
            var Q0;
            Q0 = qSketchRegion(id + "F5", true);
            extrude(context, id + "F6", {"entities" : qUnion([Q0]), "depth" : 2 * mm, "offsetDistance" : 25 * mm});
        }
        {
            var Q0;
            Q0=qCreatedBy(makeId("Top.planeOp"),FACE);
            var sketch = newSketch(context, id + "F7", { "sketchPlane" : qUnion([Q0])});
            skArc(sketch, "E77", {"start": v(10, 32.05) * mm, "mid": v(2.75, 16.73) * mm, "end": v(0, 0) * mm});
            skArc(sketch, "E78", {"start": v(19.25, 3.58) * mm, "mid": v(16.4, 18.4) * mm, "end": v(10, 32.05) * mm});
            skFitSpline(sketch, "E79", {"points": [v(19.25, 3.58) * mm, v(17.29, 7.18) * mm, v(15.43, 10.15) * mm, v(14.23, 11.51) * mm, v(13.29, 12.2) * mm, v(11.98, 12.12) * mm, v(10.29, 11.18) * mm, v(5.93, 7.51) * mm, v(2.46, 3.58) * mm, v(0, 0) * mm], "startDerivative": vector(-14.26, 27.94) * mm, "endDerivative": vector(-17.6, -27.28) * mm});
            skLineSegment(sketch, "E80", {"start": v(10, 26.05) * mm, "end": v(11.15, 19.46) * mm});
            skLineSegment(sketch, "E81", {"start": v(11.15, 19.46) * mm, "end": v(12.75, 18.65) * mm});
            skLineSegment(sketch, "E82", {"start": v(12.75, 18.65) * mm, "end": v(11.15, 17.82) * mm});
            skLineSegment(sketch, "E83", {"start": v(11.15, 17.82) * mm, "end": v(11.7, 14.7) * mm});
            skLineSegment(sketch, "E84", {"start": v(11.7, 14.7) * mm, "end": v(10, 16.94) * mm});
            skLineSegment(sketch, "E85", {"start": v(10, 16.94) * mm, "end": v(10, 18.42) * mm});
            skLineSegment(sketch, "E86.MirrorCS", {"start": v(10, 26.05) * mm, "end": v(8.85, 19.46) * mm});
            skLineSegment(sketch, "E87.MirrorCS", {"start": v(8.85, 19.46) * mm, "end": v(7.25, 18.65) * mm});
            skLineSegment(sketch, "E88.MirrorCS", {"start": v(7.25, 18.65) * mm, "end": v(8.85, 17.82) * mm});
            skLineSegment(sketch, "E89.MirrorCS", {"start": v(8.85, 17.82) * mm, "end": v(8.3, 14.7) * mm});
            skLineSegment(sketch, "E90.MirrorCS", {"start": v(8.3, 14.7) * mm, "end": v(10, 16.94) * mm});
            skSolve(sketch);
        }
        {
            var Q0;
            Q0 = qSketchRegion(id + "F7", true);
            extrude(context, id + "F8", {"entities" : qUnion([Q0]), "operationType" : NewBodyOperationType.ADD, "depth" : 3 * mm, "offsetDistance" : 25 * mm});
        }
        {
            var Q0;
            Q0=qCreatedBy(makeId("Right.planeOp"),FACE);
            var sketch = newSketch(context, id + "F9", { "sketchPlane" : qUnion([Q0])});
            skLineSegment(sketch, "E91", {"start": v(42.05, 9.07) * mm, "end": v(-10, 9.07) * mm});
            skLineSegment(sketch, "E92", {"start": v(42.05, 9.07) * mm, "end": v(42.05, 0.5) * mm});
            skLineSegment(sketch, "E93", {"start": v(-10, 9.07) * mm, "end": v(-10, 0.5) * mm});
            skArc(sketch, "E94", {"start": v(42.05, 0.5) * mm, "mid": v(16.03, 2.94) * mm, "end": v(-10, 0.5) * mm});
            skSolve(sketch);
        }
        {
            var Q0;
            Q0 = qSketchRegion(id + "F9", true);
            extrude(context, id + "F10", {"entities" : qUnion([Q0]), "operationType" : NewBodyOperationType.REMOVE, "depth" : 100 * mm, "offsetDistance" : 25 * mm});
        }
        {
            var Q0;
            Q0=makeQuery(id+"F10.boolean.opBoolean","INTERSECT",EDGE,{"derivedFrom":[makeQuery(id+"F8.boolean.opBoolean","MERGE",FACE,{"derivedFrom":[makeQuery(id+"F6.opExtrude","SWEPT_FACE",FACE,{"disambiguationData":[OSD([sQuery(id+"F5.wireOp",EDGE,"E75")])]}),makeQuery(id+"F8.opExtrude","SWEPT_FACE",FACE,{"disambiguationData":[OSD([sQuery(id+"F7.wireOp",EDGE,"E78")])]})]}),makeQuery(id+"F10.opExtrude","SWEPT_FACE",FACE,{"disambiguationData":[OSD([sQuery(id+"F9.wireOp",EDGE,"E94")])]})]});
            var Q1;
            Q1=makeQuery(id+"F10.boolean.opBoolean","INTERSECT",EDGE,{"derivedFrom":[makeQuery(id+"F8.boolean.opBoolean","MERGE",FACE,{"derivedFrom":[makeQuery(id+"F6.opExtrude","SWEPT_FACE",FACE,{"disambiguationData":[OSD([sQuery(id+"F5.wireOp",EDGE,"E74")])]}),makeQuery(id+"F8.opExtrude","SWEPT_FACE",FACE,{"disambiguationData":[OSD([sQuery(id+"F7.wireOp",EDGE,"E77")])]})]}),makeQuery(id+"F10.opExtrude","SWEPT_FACE",FACE,{"disambiguationData":[OSD([sQuery(id+"F9.wireOp",EDGE,"E94")])]})]});
            var Q2;
            Q2=makeQuery(id+"F10.boolean.opBoolean","INTERSECT",EDGE,{"derivedFrom":[makeQuery(id+"F8.boolean.opBoolean","MERGE",FACE,{"derivedFrom":[makeQuery(id+"F6.opExtrude","SWEPT_FACE",FACE,{"disambiguationData":[OSD([sQuery(id+"F5.wireOp",EDGE,"E76")])]}),makeQuery(id+"F8.opExtrude","SWEPT_FACE",FACE,{"disambiguationData":[OSD([sQuery(id+"F7.wireOp",EDGE,"E79")])]})]}),makeQuery(id+"F10.opExtrude","SWEPT_FACE",FACE,{"disambiguationData":[OSD([sQuery(id+"F9.wireOp",EDGE,"E94")])]})]});
            fillet(context, id + "F11", {"entities" : qUnion([Q0, Q1, Q2]), "tangentPropagation" : true, "radius" : 0.6 * mm, "defaultsChanged" : true, "vertexSettings" : [], "allowEdgeOverflow" : false});
        }
        {
            var Q0;
            Q0=makeQuery(id+"F7.imprint","IMPRINT",FACE,{"disambiguationData":[TD([[makeQuery(id+"F7.imprint","IMPRINT",EDGE,{"derivedFrom":sQuery(id+"F7.wireOp",EDGE,"E77")}),1.0]])]});
            var sketch = newSketch(context, id + "F12", { "sketchPlane" : qUnion([Q0])});
            skCircle(sketch, "E95", {"center": v(9.93, 18.42) * mm, "radius": 2.1 * mm});
            skSolve(sketch);
        }
        {
            var Q0;
            Q0 = qSketchRegion(id + "F12", true);
            extrude(context, id + "F13", {"entities" : qUnion([Q0]), "operationType" : NewBodyOperationType.REMOVE, "depth" : 1.5 * mm, "offsetDistance" : 25 * mm});
        }
        {
            var Q0;
            Q0=makeQuery(id+"F10.boolean.opBoolean","INTERSECT",EDGE,{"derivedFrom":[makeQuery(id+"F8.opExtrude","SWEPT_FACE",FACE,{"disambiguationData":[OSD([sQuery(id+"F7.wireOp",EDGE,"yVgh9X9Y-4TfN-GKj7-fGmn-d1CRGFCxaC6K")])]}),makeQuery(id+"F10.opExtrude","SWEPT_FACE",FACE,{"disambiguationData":[OSD([sQuery(id+"F9.wireOp",EDGE,"E94")])]})]});
            var Q1;
            Q1=makeQuery(id+"F10.boolean.opBoolean","INTERSECT",EDGE,{"derivedFrom":[makeQuery(id+"F8.opExtrude","SWEPT_FACE",FACE,{"disambiguationData":[OSD([sQuery(id+"F7.wireOp",EDGE,"7feIgUNh-nRAl-lLnm-IURJ-Wqx9b08FJGzL")])]}),makeQuery(id+"F10.opExtrude","SWEPT_FACE",FACE,{"disambiguationData":[OSD([sQuery(id+"F9.wireOp",EDGE,"E94")])]})]});
            var Q2;
            Q2=makeQuery(id+"F10.boolean.opBoolean","INTERSECT",EDGE,{"derivedFrom":[makeQuery(id+"F8.opExtrude","SWEPT_FACE",FACE,{"disambiguationData":[OSD([sQuery(id+"F7.wireOp",EDGE,"6lmLKfa9-YDBl-B7fY-oXUp-0c1PHNLdVbwB")])]}),makeQuery(id+"F10.opExtrude","SWEPT_FACE",FACE,{"disambiguationData":[OSD([sQuery(id+"F9.wireOp",EDGE,"E94")])]})]});
            var Q3;
            Q3=makeQuery(id+"F10.boolean.opBoolean","INTERSECT",EDGE,{"derivedFrom":[makeQuery(id+"F8.opExtrude","SWEPT_FACE",FACE,{"disambiguationData":[OSD([sQuery(id+"F7.wireOp",EDGE,"Iuu220FR-nvCw-Eevc-bgOQ-zVjXQlc8bRa4")])]}),makeQuery(id+"F10.opExtrude","SWEPT_FACE",FACE,{"disambiguationData":[OSD([sQuery(id+"F9.wireOp",EDGE,"E94")])]})]});
            var Q4;
            Q4=makeQuery(id+"F10.boolean.opBoolean","INTERSECT",EDGE,{"derivedFrom":[makeQuery(id+"F8.opExtrude","SWEPT_FACE",FACE,{"disambiguationData":[OSD([sQuery(id+"F7.wireOp",EDGE,"AvQXQWCP-Lblw-EsRI-yvdM-FFXgrwUr3cUu")])]}),makeQuery(id+"F10.opExtrude","SWEPT_FACE",FACE,{"disambiguationData":[OSD([sQuery(id+"F9.wireOp",EDGE,"E94")])]})]});
            var Q5;
            Q5=makeQuery(id+"F10.boolean.opBoolean","INTERSECT",EDGE,{"derivedFrom":[makeQuery(id+"F8.opExtrude","SWEPT_FACE",FACE,{"disambiguationData":[OSD([sQuery(id+"F7.wireOp",EDGE,"eb419513-5c57-42cb-bc96-a34a9ca713420.MirrorCS")])]}),makeQuery(id+"F10.opExtrude","SWEPT_FACE",FACE,{"disambiguationData":[OSD([sQuery(id+"F9.wireOp",EDGE,"E94")])]})]});
            var Q6;
            Q6=makeQuery(id+"F10.boolean.opBoolean","INTERSECT",EDGE,{"derivedFrom":[makeQuery(id+"F8.opExtrude","SWEPT_FACE",FACE,{"disambiguationData":[OSD([sQuery(id+"F7.wireOp",EDGE,"f4878ecd-d4a4-471e-9c98-345369be92b90.MirrorCS")])]}),makeQuery(id+"F10.opExtrude","SWEPT_FACE",FACE,{"disambiguationData":[OSD([sQuery(id+"F9.wireOp",EDGE,"E94")])]})]});
            var Q7;
            Q7=makeQuery(id+"F10.boolean.opBoolean","INTERSECT",EDGE,{"derivedFrom":[makeQuery(id+"F8.opExtrude","SWEPT_FACE",FACE,{"disambiguationData":[OSD([sQuery(id+"F7.wireOp",EDGE,"f887dc1c-5a2c-4499-bcbe-b27c71822e440.MirrorCS")])]}),makeQuery(id+"F10.opExtrude","SWEPT_FACE",FACE,{"disambiguationData":[OSD([sQuery(id+"F9.wireOp",EDGE,"E94")])]})]});
            var Q8;
            Q8=makeQuery(id+"F10.boolean.opBoolean","INTERSECT",EDGE,{"derivedFrom":[makeQuery(id+"F8.opExtrude","SWEPT_FACE",FACE,{"disambiguationData":[OSD([sQuery(id+"F7.wireOp",EDGE,"72353e7c-8228-480c-b59f-182cc749947c0.MirrorCS")])]}),makeQuery(id+"F10.opExtrude","SWEPT_FACE",FACE,{"disambiguationData":[OSD([sQuery(id+"F9.wireOp",EDGE,"E94")])]})]});
            var Q9;
            Q9=makeQuery(id+"F13.boolean.opBoolean","COPY",EDGE,{"derivedFrom":makeQuery(id+"F13.opExtrude","CAP_EDGE",EDGE,{"disambiguationData":[OSD([sQuery(id+"F12.wireOp",EDGE,"E95")])],"isStart":true})});
            var Q10;
            Q10=makeQuery(id+"F6.opExtrude","CAP_FACE",FACE,{"disambiguationData":[OSD([sQuery(id+"F5.wireOp",EDGE,"E74"),sQuery(id+"F5.wireOp",EDGE,"E75"),sQuery(id+"F5.wireOp",EDGE,"E76")])],"isStart":true});
            chamfer(context, id + "F14", {"entities" : qUnion([Q0, Q1, Q2, Q3, Q4, Q5, Q6, Q7, Q8, Q9, Q10]), "width" : 0.4 * mm, "tangentPropagation" : true});
        }
    });
